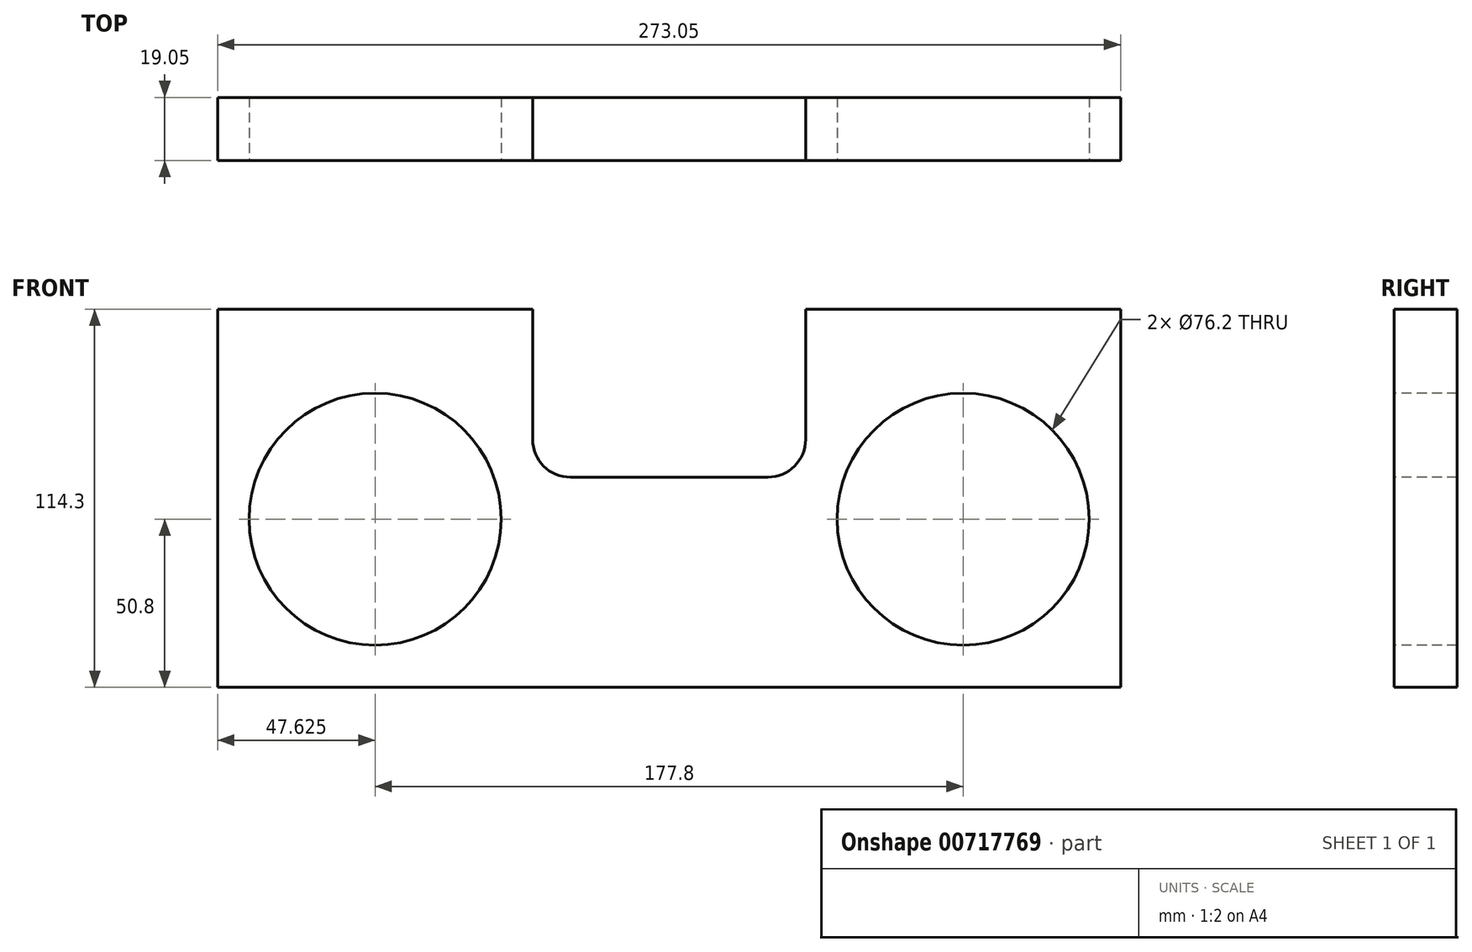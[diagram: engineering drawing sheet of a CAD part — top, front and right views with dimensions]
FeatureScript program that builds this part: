
annotation { "Feature Type Name" : "Feature", "Feature Type Description" : "" }
export const myFeature = defineFeature(function(context is Context, id is Id, definition is map)
    precondition{}
    {
        {
            var Q0;
            Q0=qCreatedBy(makeId("Front.planeOp"),FACE);
            var sketch = newSketch(context, id + "F0", { "sketchPlane" : qUnion([Q0])});
            skLineSegment(sketch, "E0.bottom", {"start": v(0, 0) * mm, "end": v(273.05, 0) * mm});
            skLineSegment(sketch, "E0.top", {"start": v(0, 114.3) * mm, "end": v(273.05, 114.3) * mm});
            skLineSegment(sketch, "E0.left", {"start": v(0, 0) * mm, "end": v(0, 114.3) * mm});
            skLineSegment(sketch, "E0.right", {"start": v(273.05, 0) * mm, "end": v(273.05, 114.3) * mm});
            skSolve(sketch);
        }
        {
            var Q0;
            Q0=qSketchRegion(id+"F0",true);
            extrude(context, id + "F1", {"entities" : qUnion([Q0]), "depth" : 19.05 * mm, "offsetDistance" : 25.4 * mm});
        }
        {
            var Q0;
            Q0=makeQuery(id+"F1.opExtrude","CAP_FACE",FACE,{"disambiguationData":[OSD([sQuery(id+"F0.wireOp",EDGE,"E0.bottom"),sQuery(id+"F0.wireOp",EDGE,"E0.top"),sQuery(id+"F0.wireOp",EDGE,"E0.left"),sQuery(id+"F0.wireOp",EDGE,"E0.right")])],"isStart":false});
            var sketch = newSketch(context, id + "F2", { "sketchPlane" : qUnion([Q0])});
            skCircle(sketch, "E1", {"center": v(47.63, 50.8) * mm, "radius": 38.1 * mm});
            skCircle(sketch, "E2", {"center": v(225.43, 50.8) * mm, "radius": 38.1 * mm});
            skPoint(sketch, "E2.centerSnap0", {"position": v(273.05, 50.8) * mm});
            skSolve(sketch);
        }
        {
            var Q0;
            Q0=makeQuery(id+"F2.imprint","IMPRINT",FACE,{"disambiguationData":[TD([[makeQuery(id+"F2.imprint","IMPRINT",EDGE,{"derivedFrom":sQuery(id+"F2.wireOp",EDGE,"E1")}),1.0]])]});
            var Q1;
            Q1=makeQuery(id+"F2.imprint","IMPRINT",FACE,{"disambiguationData":[TD([[makeQuery(id+"F2.imprint","IMPRINT",EDGE,{"derivedFrom":sQuery(id+"F2.wireOp",EDGE,"E2")}),1.0]])]});
            extrude(context, id + "F3", {"entities" : qUnion([Q0, Q1]), "operationType" : NewBodyOperationType.REMOVE, "oppositeDirection" : true, "depth" : 25.4 * mm, "offsetDistance" : 25.4 * mm});
        }
        {
            var Q0;
            Q0=makeQuery(id+"F1.opExtrude","CAP_FACE",FACE,{"disambiguationData":[OSD([sQuery(id+"F0.wireOp",EDGE,"E0.bottom"),sQuery(id+"F0.wireOp",EDGE,"E0.top"),sQuery(id+"F0.wireOp",EDGE,"E0.left"),sQuery(id+"F0.wireOp",EDGE,"E0.right")])],"isStart":false});
            var sketch = newSketch(context, id + "F4", { "sketchPlane" : qUnion([Q0])});
            skLineSegment(sketch, "E3.bottom", {"start": v(95.25, 114.3) * mm, "end": v(177.8, 114.3) * mm});
            skLineSegment(sketch, "E3.top", {"start": v(106.68, 63.5) * mm, "end": v(166.37, 63.5) * mm});
            skLineSegment(sketch, "E3.left", {"start": v(95.25, 114.3) * mm, "end": v(95.25, 74.93) * mm});
            skLineSegment(sketch, "E3.right", {"start": v(177.8, 114.3) * mm, "end": v(177.8, 74.93) * mm});
            skPoint(sketch, "E4.visualSharp", {"position": v(95.25, 63.5) * mm});
            skArc(sketch, "E4.filletArc", {"start": v(95.25, 74.93) * mm, "mid": v(98.6, 66.85) * mm, "end": v(106.68, 63.5) * mm});
            skPoint(sketch, "E5.visualSharp", {"position": v(177.8, 63.5) * mm});
            skArc(sketch, "E5.filletArc", {"start": v(166.37, 63.5) * mm, "mid": v(174.45, 66.85) * mm, "end": v(177.8, 74.93) * mm});
            skSolve(sketch);
        }
        {
            var Q0;
            Q0=makeQuery(id+"F4.imprint","IMPRINT",FACE,{"disambiguationData":[TD([[makeQuery(id+"F4.imprint","IMPRINT",EDGE,{"derivedFrom":sQuery(id+"F4.wireOp",EDGE,"E3.bottom")}),-1.0]])]});
            extrude(context, id + "F5", {"entities" : qUnion([Q0]), "operationType" : NewBodyOperationType.REMOVE, "oppositeDirection" : true, "depth" : 25.4 * mm, "offsetDistance" : 25.4 * mm});
        }
    });
